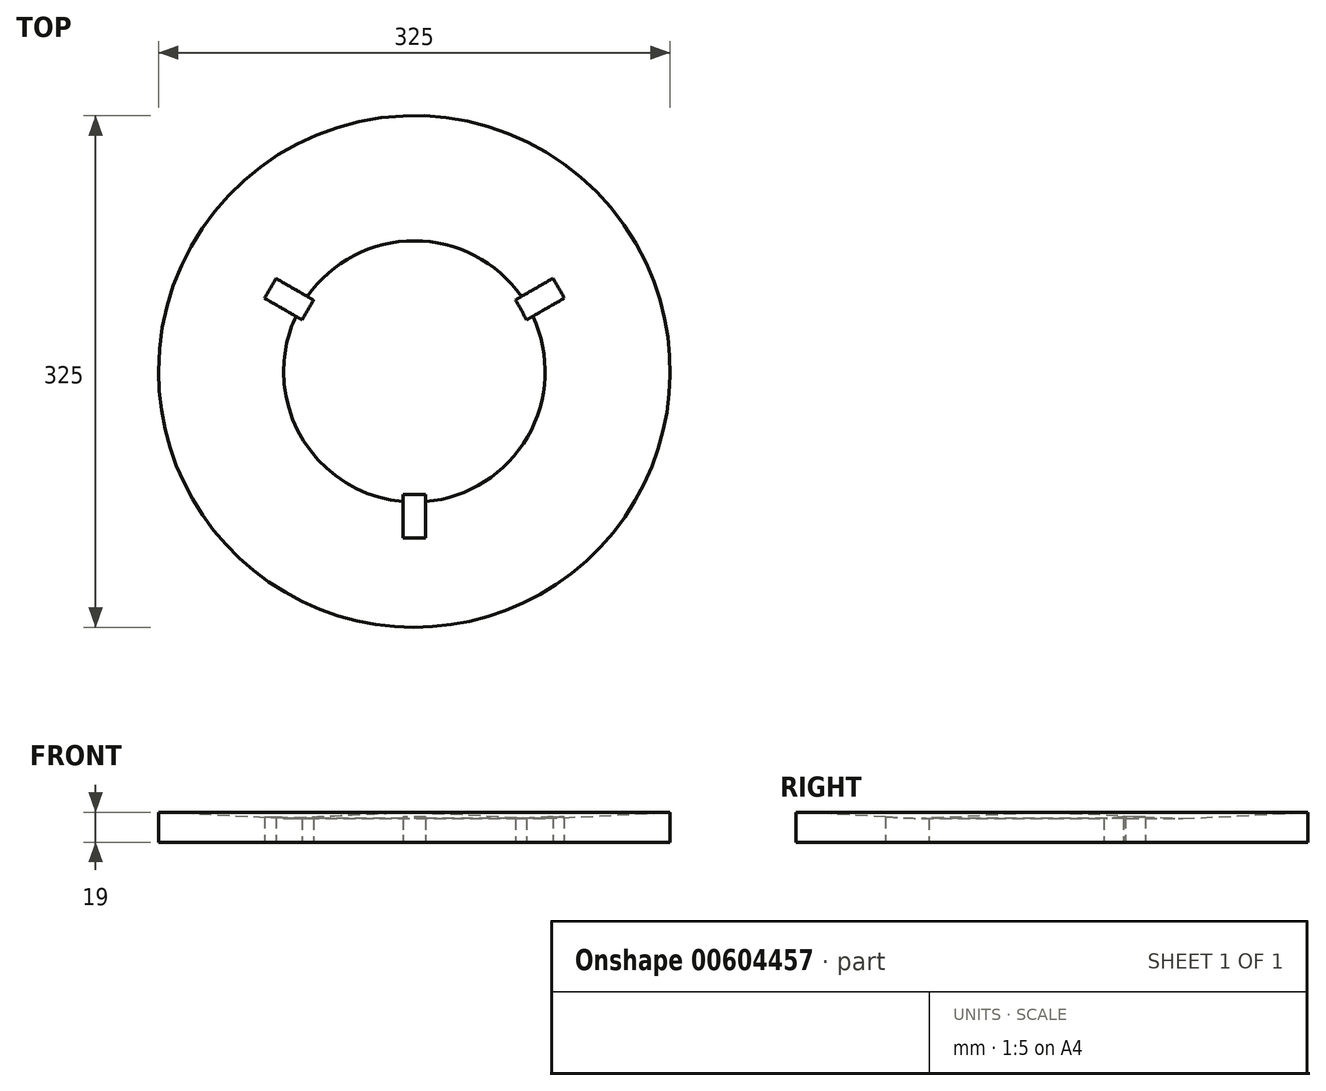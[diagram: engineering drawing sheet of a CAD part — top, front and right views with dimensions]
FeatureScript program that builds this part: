
annotation { "Feature Type Name" : "Feature", "Feature Type Description" : "" }
export const myFeature = defineFeature(function(context is Context, id is Id, definition is map)
    precondition{}
    {
        {
            var Q0;
            Q0=qCreatedBy(makeId("Front.planeOp"),FACE);
            var sketch = newSketch(context, id + "F0", { "sketchPlane" : qUnion([Q0])});
            skLineSegment(sketch, "E0", {"start": v(0, 0) * mm, "end": v(-162.5, 0) * mm});
            skLineSegment(sketch, "E1", {"start": v(0, 0) * mm, "end": v(0, 19) * mm});
            skLineSegment(sketch, "E2", {"start": v(-83, 15) * mm, "end": v(0, 19) * mm});
            skLineSegment(sketch, "E3", {"start": v(-162.5, 0) * mm, "end": v(-162.5, 19) * mm});
            skLineSegment(sketch, "E4", {"start": v(-162.5, 19) * mm, "end": v(-83, 15) * mm});
            skLineSegment(sketch, "E5.MirrorCS", {"start": v(83, 15) * mm, "end": v(0, 19) * mm});
            skLineSegment(sketch, "E6.MirrorCS", {"start": v(0, 0) * mm, "end": v(162.5, 0) * mm});
            skLineSegment(sketch, "E7.MirrorCS", {"start": v(162.5, 0) * mm, "end": v(162.5, 19) * mm});
            skLineSegment(sketch, "E8.MirrorCS", {"start": v(162.5, 19) * mm, "end": v(83, 15) * mm});
            skSolve(sketch);
        }
        {
            var Q0;
            Q0=makeQuery(id+"F0.imprint","IMPRINT",FACE,{"disambiguationData":[TD([[makeQuery(id+"F0.imprint","IMPRINT",EDGE,{"derivedFrom":sQuery(id+"F0.wireOp",EDGE,"E1")}),-1.0]])]});
            var Q1;
            Q1=sQuery(id+"F0.wireOp",EDGE,"E1");
            revolve(context, id + "F1", {"entities" : qUnion([Q0]), "axis" : qUnion([Q1]), "revolveType" : RevolveType.FULL});
        }
        {
            var Q0;
            Q0=makeQuery(id+"F1.opRevolve","SWEPT_FACE",FACE,{"disambiguationData":[OSD([sQuery(id+"F0.wireOp",EDGE,"E6.MirrorCS")])]});
            var sketch = newSketch(context, id + "F2", { "sketchPlane" : qUnion([Q0])});
            skLineSegment(sketch, "E9.bottom", {"start": v(7.25, 105.75) * mm, "end": v(-7.25, 105.75) * mm});
            skLineSegment(sketch, "E9.top", {"start": v(7.25, 78.25) * mm, "end": v(-7.25, 78.25) * mm});
            skLineSegment(sketch, "E9.left", {"start": v(7.25, 105.75) * mm, "end": v(7.25, 78.25) * mm});
            skLineSegment(sketch, "E9.right", {"start": v(-7.25, 105.75) * mm, "end": v(-7.25, 78.25) * mm});
            skPoint(sketch, "E9.middle", {"position": v(0, 92) * mm});
            skLineSegment(sketch, "E10.1.0", {"start": v(-95.2, -46.6) * mm, "end": v(-71.4, -32.85) * mm});
            skLineSegment(sketch, "E10.1.1", {"start": v(-95.2, -46.6) * mm, "end": v(-87.96, -59.15) * mm});
            skLineSegment(sketch, "E10.1.2", {"start": v(-87.96, -59.15) * mm, "end": v(-64.14, -45.4) * mm});
            skLineSegment(sketch, "E10.1.3", {"start": v(-71.4, -32.85) * mm, "end": v(-64.14, -45.4) * mm});
            skLineSegment(sketch, "E10.2.0", {"start": v(87.96, -59.15) * mm, "end": v(64.14, -45.4) * mm});
            skLineSegment(sketch, "E10.2.1", {"start": v(87.96, -59.15) * mm, "end": v(95.2, -46.6) * mm});
            skLineSegment(sketch, "E10.2.2", {"start": v(95.2, -46.6) * mm, "end": v(71.4, -32.85) * mm});
            skLineSegment(sketch, "E10.2.3", {"start": v(64.14, -45.4) * mm, "end": v(71.4, -32.85) * mm});
            skPoint(sketch, "E10.center", {"position": v(0, 0) * mm});
            skSolve(sketch);
        }
        {
            var Q0;
            Q0 = qSketchRegion(id + "F2", true);
            extrude(context, id + "F3", {"entities" : qUnion([Q0]), "operationType" : NewBodyOperationType.REMOVE, "endBound" : BoundingType.UP_TO_NEXT, "oppositeDirection" : true, "depth" : 25 * mm, "offsetDistance" : 25 * mm});
        }
    });
